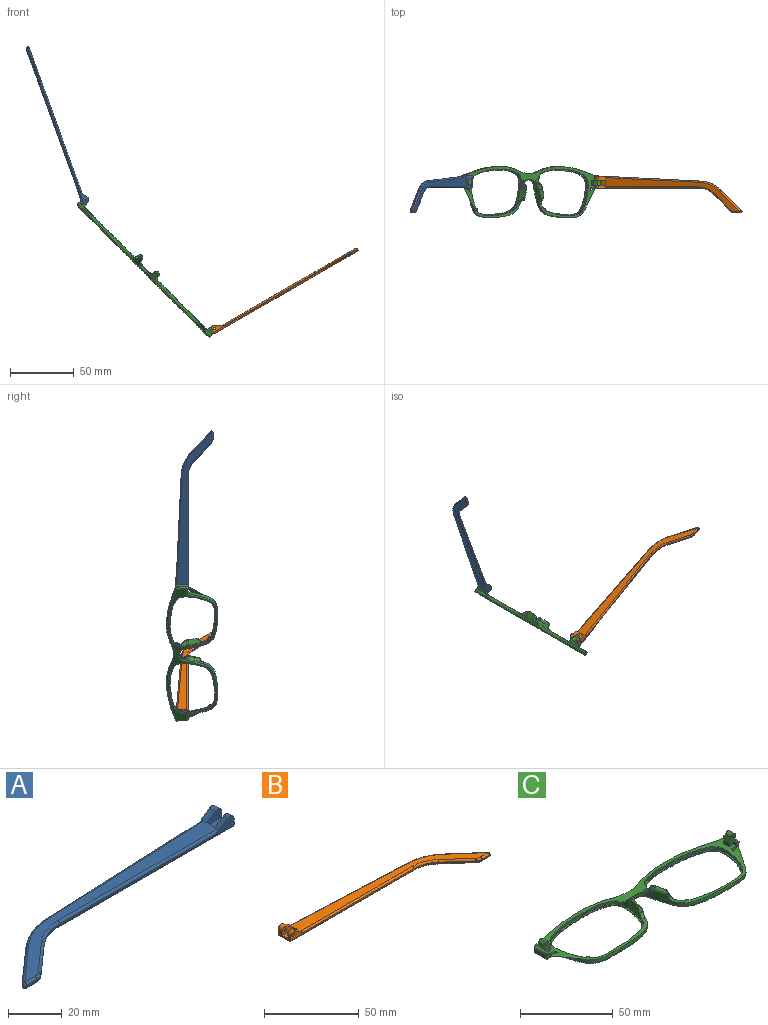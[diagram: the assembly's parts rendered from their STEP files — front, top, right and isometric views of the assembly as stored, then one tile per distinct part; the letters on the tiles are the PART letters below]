
ASSEMBLY  parts=3 mates=2
PART A: 43 faces, bbox 130.2x29.5x5.9 mm
  f0: plane 9.62x3.72mm, normal (1,0,0), area 24.7mm2, adj f1,f3,f4,f5,f10,f16,f18,f28
  f1: cylinder r=2.2mm len=3.45mm, axis (0,-1,0), area 11mm2, adj f0,f2,f4,f37
  f2: plane 6.01x3.91mm, normal (-0.55,0,0.84), area 12.7mm2, adj f1,f4,f9,f19,f37
  f3: plane 2.26x0.1mm, normal (0,0,1), area 0.1mm2, adj f0,f5,f18
  f4: plane 92.1x4.9mm, normal (0,-1,0), area 79.9mm2, adj f0,f1,f2,f14,f19,f36,f42
  f5: plane 93.42x4.13mm, normal (-0.04,1,0), area 64.8mm2, adj f0,f3,f11,f15,f17,f27,f28
  f6: plane 17.82x15.72mm, normal (-0.66,0.75,0), area 14.3mm2, adj f11,f12,f25,f30
  f7: plane 5.46x0.6mm, normal (0,-1,0), area 3.3mm2, adj f12,f13,f23,f32
  f8: plane 14.99x13.23mm, normal (0.66,-0.75,0), area 12mm2, adj f13,f14,f21,f34
  f9: plane 121.18x26.73mm, normal (0,0,1), area 627.7mm2, adj f2,f17,f19,f20,f21,f22,f23,f25
  f10: plane 129.1x27.08mm, normal (0,0,-1), area 686.5mm2, adj f0,f28,f29,f30,f32,f33,f34,f35
  f11: cylinder r=30mm len=18.52mm, axis (0,0,-1), area 12.2mm2, adj f5,f6,f26,f29
  f12: cylinder r=1mm len=1.75mm, axis (0,0,-1), area 1.5mm2, adj f6,f7,f24,f31
  f13: cylinder r=5mm len=3.31mm, axis (0,0,-1), area 2.2mm2, adj f7,f8,f22,f33
  f14: cylinder r=20mm len=13.23mm, axis (0,0,1), area 8.7mm2, adj f4,f8,f20,f35
  f15: plane 5.66x0.25mm, normal (0,0,-1), area 0.7mm2, adj f5,f17,f18
  f16: cylinder r=2.2mm len=3.45mm, axis (0,-1,0), area 14.8mm2, adj f0,f17,f18,f38
  f17: plane 6.01x3.91mm, normal (-0.55,0,0.84), area 16.9mm2, adj f5,f9,f15,f16,f18,f27,f38
  f18: plane 7.92x3.3mm, normal (0,1,0), area 15.9mm2, adj f0,f3,f15,f16,f17,f41
  f19: cylinder r=1mm len=84.18mm, axis (-1,0,0), area 131.4mm2, adj f2,f4,f9,f20
  f20: torus R=21mm, axis (0,0,1), area 23.1mm2, adj f9,f14,f19,f21
  f21: cylinder r=1mm len=15.65mm, axis (-0.75,-0.66,0), area 31.4mm2, adj f8,f9,f20,f22
  f22: torus R=4mm, axis (0,0,1), area 5.3mm2, adj f9,f13,f21,f23
  f23: cylinder r=1mm len=5.46mm, axis (-1,0,0), area 8.6mm2, adj f7,f9,f22,f24
  f24: sphere r=1mm, area 2.4mm2, adj f12,f23,f25
  f25: cylinder r=1mm len=18.48mm, axis (0.75,0.66,0), area 37.3mm2, adj f6,f9,f24,f26
  f26: torus R=29mm, axis (0,0,1), area 31.6mm2, adj f9,f11,f25,f27
  f27: cylinder r=1mm len=85.5mm, axis (1,0.04,0), area 133.5mm2, adj f5,f9,f17,f26
  f28: cylinder r=1mm len=93.46mm, axis (-1,-0.04,0), area 146.9mm2, adj f0,f5,f10,f29
  f29: torus R=29mm, axis (0,0,1), area 31.6mm2, adj f10,f11,f28,f30
  f30: cylinder r=1mm len=18.48mm, axis (-0.75,-0.66,0), area 37.3mm2, adj f6,f10,f29,f31
  f31: sphere r=1mm, area 2.4mm2, adj f12,f30,f32
  f32: cylinder r=1mm len=5.46mm, axis (1,0,0), area 8.6mm2, adj f7,f10,f31,f33
  f33: torus R=4mm, axis (0,0,1), area 5.3mm2, adj f10,f13,f32,f34
  f34: cylinder r=1mm len=15.65mm, axis (0.75,0.66,0), area 31.4mm2, adj f8,f10,f33,f35
  f35: torus R=21mm, axis (0,0,1), area 23.1mm2, adj f10,f14,f34,f36
  f36: cylinder r=1mm len=92.1mm, axis (1,0,0), area 144.7mm2, adj f0,f4,f10,f35
  f37: plane 7.92x4.7mm, normal (0,1,0), area 27mm2, adj f0,f1,f2,f39,f40,f42
  f38: plane 7.92x4.7mm, normal (0,-1,0), area 27mm2, adj f0,f16,f17,f39,f40,f41
  f39: plane 7.92x4.1mm, normal (0,0,1), area 32.5mm2, adj f0,f37,f38,f40
  f40: plane 4.1x1.4mm, normal (1,0,0), area 5.7mm2, adj f9,f37,f38,f39
  f41: cylinder r=0.5mm len=3.1mm, axis (0,-1,0), area 9.7mm2, adj f18,f38
  f42: cylinder r=0.5mm len=2.3mm, axis (0,-1,0), area 7.2mm2, adj f4,f37
PART B: 43 faces, bbox 130.2x29.5x5.9 mm
  f0: plane 9.62x3.72mm, normal (-1,0,0), area 24.7mm2, adj f1,f3,f4,f5,f10,f16,f18,f28
  f1: cylinder r=2.2mm len=3.45mm, axis (0,-1,0), area 11mm2, adj f0,f2,f4,f37
  f2: plane 6.01x3.91mm, normal (0.55,0,0.84), area 12.7mm2, adj f1,f4,f9,f19,f37
  f3: plane 2.26x0.1mm, normal (0,0,1), area 0.1mm2, adj f0,f5,f18
  f4: plane 92.1x4.9mm, normal (0,-1,0), area 78.2mm2, adj f0,f1,f2,f14,f19,f36,f42
  f5: plane 93.42x4.13mm, normal (0.04,1,0), area 64.8mm2, adj f0,f3,f11,f15,f17,f27,f28
  f6: plane 17.82x15.72mm, normal (0.66,0.75,0), area 14.3mm2, adj f11,f12,f25,f30
  f7: plane 5.46x0.6mm, normal (0,-1,0), area 3.3mm2, adj f12,f13,f23,f32
  f8: plane 14.99x13.23mm, normal (-0.66,-0.75,0), area 12mm2, adj f13,f14,f21,f34
  f9: plane 121.18x26.73mm, normal (0,0,1), area 627.7mm2, adj f2,f17,f19,f20,f21,f22,f23,f25
  f10: plane 129.1x27.08mm, normal (0,0,-1), area 686.5mm2, adj f0,f28,f29,f30,f32,f33,f34,f35
  f11: cylinder r=30mm len=18.52mm, axis (0,0,-1), area 12.2mm2, adj f5,f6,f26,f29
  f12: cylinder r=1mm len=1.75mm, axis (0,0,-1), area 1.5mm2, adj f6,f7,f24,f31
  f13: cylinder r=5mm len=3.31mm, axis (0,0,-1), area 2.2mm2, adj f7,f8,f22,f33
  f14: cylinder r=20mm len=13.23mm, axis (0,0,1), area 8.7mm2, adj f4,f8,f20,f35
  f15: plane 5.66x0.25mm, normal (0,0,-1), area 0.7mm2, adj f5,f17,f18
  f16: cylinder r=2.2mm len=3.45mm, axis (0,-1,0), area 14.8mm2, adj f0,f17,f18,f38
  f17: plane 6.01x3.91mm, normal (0.55,0,0.84), area 16.9mm2, adj f5,f9,f15,f16,f18,f27,f38
  f18: plane 7.92x3.3mm, normal (0,1,0), area 14.3mm2, adj f0,f3,f15,f16,f17,f41
  f19: cylinder r=1mm len=84.18mm, axis (1,0,0), area 131.4mm2, adj f2,f4,f9,f20
  f20: torus R=21mm, axis (0,0,1), area 23.1mm2, adj f9,f14,f19,f21
  f21: cylinder r=1mm len=15.65mm, axis (0.75,-0.66,0), area 31.4mm2, adj f8,f9,f20,f22
  f22: torus R=4mm, axis (0,0,1), area 5.3mm2, adj f9,f13,f21,f23
  f23: cylinder r=1mm len=5.46mm, axis (1,0,0), area 8.6mm2, adj f7,f9,f22,f24
  f24: sphere r=1mm, area 2.4mm2, adj f12,f23,f25
  f25: cylinder r=1mm len=18.48mm, axis (-0.75,0.66,0), area 37.3mm2, adj f6,f9,f24,f26
  f26: torus R=29mm, axis (0,0,1), area 31.6mm2, adj f9,f11,f25,f27
  f27: cylinder r=1mm len=85.5mm, axis (-1,0.04,0), area 133.5mm2, adj f5,f9,f17,f26
  f28: cylinder r=1mm len=93.46mm, axis (1,-0.04,0), area 146.9mm2, adj f0,f5,f10,f29
  f29: torus R=29mm, axis (0,0,1), area 31.6mm2, adj f10,f11,f28,f30
  f30: cylinder r=1mm len=18.48mm, axis (0.75,-0.66,0), area 37.3mm2, adj f6,f10,f29,f31
  f31: sphere r=1mm, area 2.4mm2, adj f12,f30,f32
  f32: cylinder r=1mm len=5.46mm, axis (-1,0,0), area 8.6mm2, adj f7,f10,f31,f33
  f33: torus R=4mm, axis (0,0,1), area 5.3mm2, adj f10,f13,f32,f34
  f34: cylinder r=1mm len=15.65mm, axis (-0.75,0.66,0), area 31.4mm2, adj f8,f10,f33,f35
  f35: torus R=21mm, axis (0,0,1), area 23.1mm2, adj f10,f14,f34,f36
  f36: cylinder r=1mm len=92.1mm, axis (-1,0,0), area 144.7mm2, adj f0,f4,f10,f35
  f37: plane 7.92x4.7mm, normal (0,1,0), area 25.4mm2, adj f0,f1,f2,f39,f40,f42
  f38: plane 7.92x4.7mm, normal (0,-1,0), area 25.4mm2, adj f0,f16,f17,f39,f40,f41
  f39: plane 7.92x4.1mm, normal (0,0,1), area 32.5mm2, adj f0,f37,f38,f40
  f40: plane 4.1x1.4mm, normal (-1,0,0), area 5.7mm2, adj f9,f37,f38,f39
  f41: cylinder r=0.88mm len=3.1mm, axis (0,-1,0), area 17mm2, adj f18,f38
  f42: cylinder r=0.88mm len=2.3mm, axis (0,-1,0), area 12.6mm2, adj f4,f37
PART C: 118 faces, bbox 148.1x40.9x18 mm
  f0: bspline ~1.82x1.22mm, area 0.7mm2, adj f2,f7,f37,f52
  f1: plane 147.73x40.5mm, normal (0,0,1), area 772.9mm2, adj f4,f5,f6,f7,f8,f12,f20,f23
  f2: bspline ~5.39x4.93mm, area 12.7mm2, adj f0,f7,f37,f41,f43,f52,f53
  f3: plane 4.46x1.45mm, normal (0,0,1), area 0.1mm2, adj f7,f38
  f4: plane 1.23x0.04mm, normal (0,0,1), area 0mm2, adj f1,f7,f22
  f5: plane 6.97x5.07mm, normal (0,1,0), area 22.7mm2, adj f1,f20,f21,f25,f27,f28,f30,f31
  f6: plane 3.2x2.36mm, normal (0,-1,0), area 5.7mm2, adj f1,f20,f26,f29
  f7: extruded ~73.26x39.84mm, area 292.7mm2, adj f0,f1,f2,f3,f4,f8,f13,f14
  f8: extruded ~35.39x5.69mm, area 72.2mm2, adj f1,f7,f18,f67
  f9: plane 144.78x37.85mm, normal (0,0,-1), area 478.1mm2, adj f13,f15,f17,f18,f19,f71,f73,f75
  f10: plane 56.31x36.53mm, normal (0,0,1), area 124.8mm2, adj f11,f19
  f11: extruded ~55.63x36.1mm, area 160.7mm2, adj f10,f12
  f12: extruded ~55.63x36.1mm, area 220.4mm2, adj f1,f11,f39,f40,f41,f42,f43,f44
  f13: bspline ~73.27x30.39mm, area 161.7mm2, adj f7,f9,f14,f71
  f14: bspline ~1x1mm, area 0.8mm2, adj f7,f13,f15
  f15: bspline ~8.99x1.23mm, area 12.6mm2, adj f7,f9,f14,f16
  f16: bspline ~1.04x1mm, area 0.7mm2, adj f7,f15,f17
  f17: bspline ~45.86x8.59mm, area 59.8mm2, adj f7,f9,f16,f18
  f18: bspline ~37.01x6.7mm, area 56.6mm2, adj f8,f9,f17,f76
  f19: bspline ~56.15x36.68mm, area 237.6mm2, adj f9,f10
  f20: plane 4x2.36mm, normal (-1,0,0), area 9.5mm2, adj f1,f5,f6,f21
  f21: plane 4x0.02mm, normal (0.34,0,0.94), area 0.1mm2, adj f5,f20,f28
  f22: plane 2.76x2.53mm, normal (0,-1,0), area 3.9mm2, adj f4,f26,f27,f35,f56
  f23: plane 7.67x1.6mm, normal (0.94,0,-0.34), area 13mm2, adj f1,f35,f36,f56
  f24: plane 2.1x1.69mm, normal (0,1,0), area 2.8mm2, adj f1,f25,f27,f36,f56
  f25: plane 3.3x2.1mm, normal (-1,0,0), area 6.9mm2, adj f1,f5,f24,f27
  f26: plane 2.35x2.1mm, normal (-1,0,0), area 4.9mm2, adj f1,f6,f22,f27,f29
  f27: plane 9.65x1.24mm, normal (0,0,1), area 8.2mm2, adj f5,f22,f24,f25,f26,f29,f30,f56
  f28: plane 4x3.31mm, normal (-0.94,0,0.34), area 14.1mm2, adj f5,f21,f29,f32
  f29: plane 5.77x5.06mm, normal (0,-1,0), area 17mm2, adj f6,f26,f27,f28,f30,f31,f32,f33
  f30: plane 4x2.21mm, normal (0.94,0,-0.34), area 9.4mm2, adj f5,f27,f29,f33
  f31: plane 4x0.01mm, normal (0.34,0,0.94), area 0mm2, adj f5,f29,f32,f33
  f32: cylinder r=1.98mm len=4mm, axis (0,1,0), area 12.4mm2, adj f5,f28,f29,f31
  f33: cylinder r=1.98mm len=4mm, axis (0,-1,0), area 12.4mm2, adj f5,f29,f30,f31
  f34: cylinder r=0.88mm len=4mm, axis (0,-1,0), area 22mm2, adj f5,f29
  f35: cone r=1mm half-angle=20deg, axis (0,0,1), area 2.3mm2, adj f1,f22,f23,f56
  f36: cylinder r=1mm len=2.28mm, axis (-0.34,0,-0.94), area 3mm2, adj f1,f23,f24,f56
  f37: extruded ~3.67x3.11mm, area 5.9mm2, adj f0,f2,f7,f59
  f38: extruded ~4.44x3.32mm, area 15.1mm2, adj f3,f7,f42,f43,f55
  f39: extruded ~4.98x1.36mm, area 6.6mm2, adj f12,f41
  f40: plane 3.63x0.97mm, normal (0,0,1), area 0.3mm2, adj f12,f41,f43
  f41: bspline ~15.5x15.35mm, area 6.4mm2, adj f2,f12,f39,f40,f54
  f42: bspline ~7.26x7.26mm, area 6.3mm2, adj f12,f38,f43,f55
  f43: bspline ~10.29x4.84mm, area 21.4mm2, adj f2,f7,f12,f38,f40,f42
  f44: plane 2.88x1.51mm, normal (0,0,-1), area 1.8mm2, adj f12,f45
  f45: cylinder r=2.28mm len=2.86mm, axis (0,0,1), area 1.8mm2, adj f1,f12,f44,f54
  f46: plane 2.5x1.83mm, normal (0,0,-1), area 1.7mm2, adj f12,f47
  f47: cylinder r=2.28mm len=2.47mm, axis (0,0,1), area 1.7mm2, adj f1,f12,f46
  f48: plane 1.79x1.31mm, normal (0,0,-1), area 0.9mm2, adj f12,f49
  f49: cylinder r=1.3mm len=1.78mm, axis (0,0,1), area 1.3mm2, adj f1,f12,f48
  f50: plane 1.95x1.68mm, normal (0,0,-1), area 1.5mm2, adj f12,f51
  f51: cylinder r=1.3mm len=1.93mm, axis (0,0,1), area 1.5mm2, adj f1,f12,f50
  f52: bspline ~2.66x2.04mm, area 1.9mm2, adj f0,f2,f7,f53,f58
  f53: bspline ~3.55x3.47mm, area 3.7mm2, adj f1,f2,f52,f54,f58
  f54: bspline ~5.1x3.97mm, area 7.6mm2, adj f1,f12,f41,f45,f53
  f55: bspline ~3.7x3.66mm, area 7.8mm2, adj f1,f7,f12,f38,f42
  f56: plane 9.71x1.44mm, normal (0.34,0,0.94), area 13.9mm2, adj f22,f23,f24,f27,f35,f36
  f57: bspline ~6.38x2.14mm, area 2.6mm2, adj f1,f7,f58,f115
  f58: bspline ~2.1x1.46mm, area 0.6mm2, adj f7,f52,f53,f57
  f59: bspline ~5.24x1.75mm, area 0mm2, adj f7,f37
  f60: bspline ~2.19x1.4mm, area 0.7mm2, adj f61,f66,f95,f110
  f61: bspline ~6.1x4.93mm, area 12.6mm2, adj f60,f66,f95,f99,f101,f110,f111
  f62: plane 4.46x1.45mm, normal (0,0,1), area 0.1mm2, adj f66,f96
  f63: plane 1.23x0.04mm, normal (0,0,1), area 0mm2, adj f1,f66,f80
  f64: plane 6.97x5.07mm, normal (0,1,0), area 22.7mm2, adj f1,f78,f79,f83,f85,f86,f88,f89
  f65: plane 3.2x2.36mm, normal (0,-1,0), area 5.7mm2, adj f1,f78,f84,f87
  f66: extruded ~73.26x39.84mm, area 292.7mm2, adj f1,f7,f60,f61,f62,f63,f67,f71
  f67: extruded ~35.39x5.69mm, area 72.2mm2, adj f1,f8,f66,f76
  f68: plane 56.31x36.53mm, normal (0,0,1), area 124.8mm2, adj f69,f77
  f69: extruded ~55.63x36.1mm, area 160.7mm2, adj f68,f70
  f70: extruded ~55.63x36.1mm, area 220.4mm2, adj f1,f69,f97,f98,f99,f100,f101,f102
  f71: bspline ~73.83x30.39mm, area 161.7mm2, adj f9,f13,f66,f72
  f72: bspline ~1x1mm, area 0.8mm2, adj f66,f71,f73
  f73: bspline ~8.99x1.23mm, area 12.6mm2, adj f9,f66,f72,f74
  f74: bspline ~1.04x1mm, area 0.8mm2, adj f66,f73,f75
  f75: bspline ~45.86x8.59mm, area 59.8mm2, adj f9,f66,f74,f76
  f76: bspline ~37.01x6.7mm, area 56.6mm2, adj f9,f18,f67,f75
  f77: bspline ~56.15x36.68mm, area 237.6mm2, adj f9,f68
  f78: plane 4x2.36mm, normal (1,0,0), area 9.5mm2, adj f1,f64,f65,f79
  f79: plane 4x0.02mm, normal (-0.34,0,0.94), area 0.1mm2, adj f64,f78,f86
  f80: plane 2.76x2.53mm, normal (0,-1,0), area 3.9mm2, adj f63,f84,f85,f93,f114
  f81: plane 7.67x1.6mm, normal (-0.94,0,-0.34), area 13mm2, adj f1,f93,f94,f114
  f82: plane 2.1x1.69mm, normal (0,1,0), area 2.8mm2, adj f1,f83,f85,f94,f114
  f83: plane 3.3x2.1mm, normal (1,0,0), area 6.9mm2, adj f1,f64,f82,f85
  f84: plane 2.35x2.1mm, normal (1,0,0), area 4.9mm2, adj f1,f65,f80,f85,f87
  f85: plane 9.65x1.24mm, normal (0,0,1), area 8.2mm2, adj f64,f80,f82,f83,f84,f87,f88,f114
  f86: plane 4x3.31mm, normal (0.94,0,0.34), area 14.1mm2, adj f64,f79,f87,f90
  f87: plane 5.77x5.06mm, normal (0,-1,0), area 17mm2, adj f65,f84,f85,f86,f88,f89,f90,f91
  f88: plane 4x2.21mm, normal (-0.94,0,-0.34), area 9.4mm2, adj f64,f85,f87,f91
  f89: plane 4x0.01mm, normal (-0.34,0,0.94), area 0mm2, adj f64,f87,f90,f91
  f90: cylinder r=1.98mm len=4mm, axis (0,1,0), area 12.4mm2, adj f64,f86,f87,f89
  f91: cylinder r=1.98mm len=4mm, axis (0,-1,0), area 12.4mm2, adj f64,f87,f88,f89
  f92: cylinder r=0.88mm len=4mm, axis (0,-1,0), area 22mm2, adj f64,f87
  f93: cone r=1mm half-angle=20deg, axis (0,0,1), area 2.3mm2, adj f1,f80,f81,f114
  f94: cylinder r=1mm len=2.28mm, axis (0.34,0,-0.94), area 3mm2, adj f1,f81,f82,f114
  f95: extruded ~3.67x3.11mm, area 5.9mm2, adj f60,f61,f66,f117
  f96: extruded ~4.44x3.32mm, area 15.1mm2, adj f62,f66,f100,f101,f113
  f97: extruded ~4.98x1.36mm, area 6.6mm2, adj f70,f99
  f98: plane 3.63x0.97mm, normal (0,0,1), area 0.3mm2, adj f70,f99,f101
  f99: bspline ~15.5x15.35mm, area 6.4mm2, adj f61,f70,f97,f98,f112
  f100: bspline ~7.26x7.26mm, area 6.2mm2, adj f70,f96,f101,f113
  f101: bspline ~10.29x4.84mm, area 21.5mm2, adj f61,f66,f70,f96,f98,f100
  f102: plane 2.88x1.51mm, normal (0,0,-1), area 1.8mm2, adj f70,f103
  f103: cylinder r=2.28mm len=2.86mm, axis (0,0,1), area 1.8mm2, adj f1,f70,f102,f112
  f104: plane 2.5x1.83mm, normal (0,0,-1), area 1.7mm2, adj f70,f105
  f105: cylinder r=2.28mm len=2.47mm, axis (0,0,1), area 1.7mm2, adj f1,f70,f104
  f106: plane 1.79x1.31mm, normal (0,0,-1), area 0.9mm2, adj f70,f107
  f107: cylinder r=1.3mm len=1.78mm, axis (0,0,1), area 1.3mm2, adj f1,f70,f106
  f108: plane 1.95x1.68mm, normal (0,0,-1), area 1.5mm2, adj f70,f109
  f109: cylinder r=1.3mm len=1.93mm, axis (0,0,1), area 1.5mm2, adj f1,f70,f108
  f110: bspline ~2.65x2.03mm, area 1.9mm2, adj f60,f61,f66,f111,f116
  f111: bspline ~3.55x3.47mm, area 3.7mm2, adj f1,f61,f110,f112,f116
  f112: bspline ~4.88x3.94mm, area 7.6mm2, adj f1,f70,f99,f103,f111
  f113: bspline ~3.7x3.66mm, area 7.8mm2, adj f1,f66,f70,f96,f100
  f114: plane 9.71x1.44mm, normal (-0.34,0,0.94), area 13.9mm2, adj f80,f81,f82,f85,f93,f94
  f115: bspline ~6.38x2.14mm, area 2.6mm2, adj f1,f57,f66,f116
  f116: bspline ~2.1x1.46mm, area 0.6mm2, adj f66,f110,f111,f115
  f117: bspline ~5.24x1.75mm, area 0mm2, adj f66,f95
PLACE A rot(axis=(0,1,0),70deg) t=(-97.58,-5.75,209.46)mm
PLACE B rot(axis=(0,-1,0),30deg) t=(-26.85,-5.75,18.97)mm
PLACE C rot(axis=(0,1,0),45deg) t=(-28.42,-1.13,99.5)mm
MATE revolute A.f1 <-> C.f90  axis (0,-1,0) through (-73.71,2.72,154.67)mm
MATE revolute B.f41 <-> C.f33  axis (0,-1,0) through (26.76,2.72,54.19)mm
